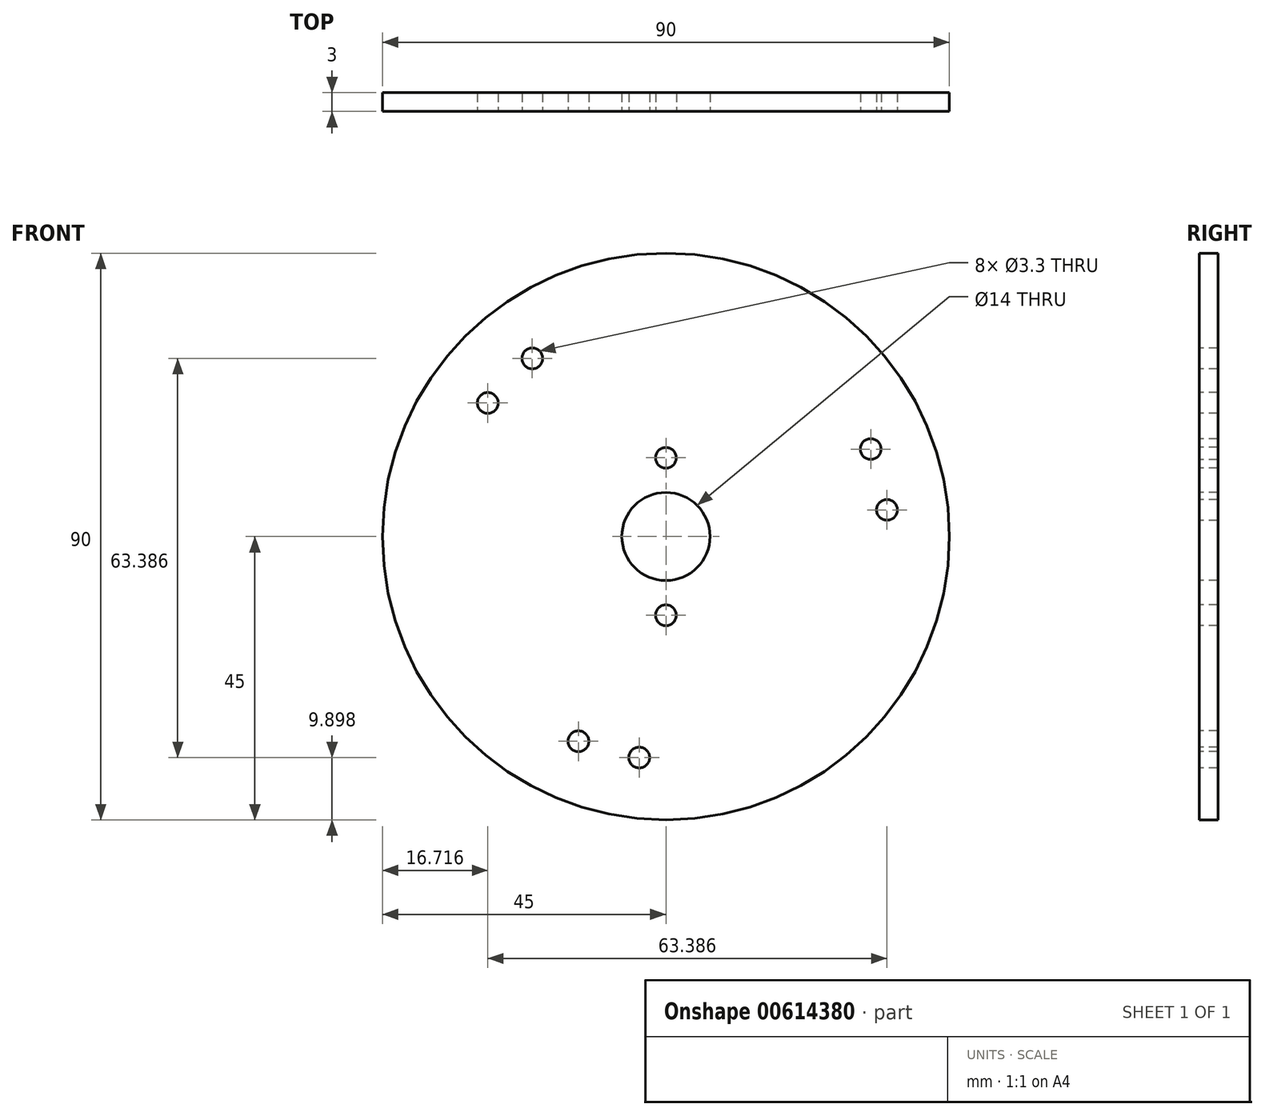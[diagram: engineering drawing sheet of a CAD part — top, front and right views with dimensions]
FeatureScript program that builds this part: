
annotation { "Feature Type Name" : "Feature", "Feature Type Description" : "" }
export const myFeature = defineFeature(function(context is Context, id is Id, definition is map)
    precondition{}
    {
        {
            var Q0;
            Q0=qCreatedBy(makeId("Front.planeOp"),FACE);
            var sketch = newSketch(context, id + "F0", { "sketchPlane" : qUnion([Q0])});
            skCircle(sketch, "E0", {"center": v(0, 0) * mm, "radius": 7 * mm});
            skCircle(sketch, "E1", {"center": v(0, 0) * mm, "radius": 45 * mm});
            skCircle(sketch, "E2", {"center": v(0, 0) * mm, "radius": 23 * mm, "construction": true});
            skLineSegment(sketch, "E3", {"start": v(0, 23) * mm, "end": v(0, 7) * mm, "construction": true});
            skPoint(sketch, "E4", {"position": v(0, 12.5) * mm});
            skPoint(sketch, "E5.1.0", {"position": v(0, -12.5) * mm});
            skLineSegment(sketch, "E6", {"start": v(0, 0) * mm, "end": v(-31.82, 31.82) * mm, "construction": true});
            skCircle(sketch, "E7", {"center": v(0, 0) * mm, "radius": 25 * mm, "construction": true});
            skCircle(sketch, "E8", {"center": v(0, 0) * mm, "radius": 18.5 * mm, "construction": true});
            skPoint(sketch, "E9", {"position": v(-21.21, 28.28) * mm});
            skPoint(sketch, "E10.MirrorP", {"position": v(-28.28, 21.21) * mm});
            skLineSegment(sketch, "E11", {"start": v(-28.28, 21.21) * mm, "end": v(-21.21, 28.28) * mm});
            skPoint(sketch, "E12", {"position": v(-24.75, 24.75) * mm});
            skPoint(sketch, "E13.1.0", {"position": v(-9.06, -33.8) * mm});
            skPoint(sketch, "E13.1.1", {"position": v(-13.89, -32.51) * mm});
            skPoint(sketch, "E13.1.2", {"position": v(-4.23, -35.1) * mm});
            skPoint(sketch, "E13.2.0", {"position": v(33.8, 9.06) * mm});
            skPoint(sketch, "E13.2.1", {"position": v(35.1, 4.23) * mm});
            skPoint(sketch, "E13.2.2", {"position": v(32.51, 13.89) * mm});
            skSolve(sketch);
        }
        {
            var Q0;
            Q0=makeQuery(id+"F0.imprint","IMPRINT",FACE,{"disambiguationData":[TD([[makeQuery(id+"F0.imprint","IMPRINT",EDGE,{"derivedFrom":sQuery(id+"F0.wireOp",EDGE,"E0")}),-1.0]])]});
            extrude(context, id + "F1", {"entities" : qUnion([Q0]), "oppositeDirection" : true, "depth" : 3 * mm, "offsetDistance" : 25 * mm});
        }
        {
            var Q0;
            Q0=sQuery(id+"F0.wireOp",VERTEX,"E9");
            var Q1;
            Q1=sQuery(id+"F0.wireOp",VERTEX,"E10.MirrorP");
            var Q2;
            Q2=sQuery(id+"F0.wireOp",VERTEX,"E13.1.1");
            var Q3;
            Q3=sQuery(id+"F0.wireOp",VERTEX,"E13.1.2");
            var Q4;
            Q4=sQuery(id+"F0.wireOp",VERTEX,"E13.2.1");
            var Q5;
            Q5=sQuery(id+"F0.wireOp",VERTEX,"E13.2.2");
            var Q6;
            Q6=makeQuery(id+"F1.opExtrude","SWEPT_BODY",BODY,{"disambiguationData":[OSD([sQuery(id+"F0.wireOp",EDGE,"E0"),sQuery(id+"F0.wireOp",EDGE,"E1")])]});
            hole(context, id + "F2", {"style" : HoleStyle.SIMPLE, "endStyle" : HoleEndStyle.THROUGH, "standardTappedOrClearance" : lookupTablePath({ "standard" : "ISO", "fit" : "Normal", "size" : "M3", "type" : "Clearance" }), "standardBlindInLast" : lookupTablePath({ "fit" : "Standard", "standard" : "ISO", "size" : "M3", "type" : "Clearance" }), "holeDiameter" : 3.3 * mm, "majorDiameter" : 5 * mm, "isTappedThrough" : true, "tappedDepth" : 12 * mm, "tapClearance" : 3, "locations" : qUnion([Q0, Q1, Q2, Q3, Q4, Q5]), "scope" : qUnion([Q6])});
        }
        {
            var Q0;
            Q0=sQuery(id+"F0.wireOp",VERTEX,"E4");
            var Q1;
            Q1=sQuery(id+"F0.wireOp",VERTEX,"E5.1.0");
            var Q2;
            Q2=makeQuery(id+"F1.opExtrude","SWEPT_BODY",BODY,{"disambiguationData":[OSD([sQuery(id+"F0.wireOp",EDGE,"E0"),sQuery(id+"F0.wireOp",EDGE,"E1")])]});
            hole(context, id + "F3", {"style" : HoleStyle.SIMPLE, "endStyle" : HoleEndStyle.THROUGH, "standardTappedOrClearance" : lookupTablePath({ "standard" : "ISO", "fit" : "Normal", "size" : "M3", "type" : "Clearance" }), "standardBlindInLast" : lookupTablePath({ "fit" : "Standard", "standard" : "ISO", "size" : "M3", "type" : "Clearance" }), "holeDiameter" : 3.3 * mm, "majorDiameter" : 5 * mm, "isTappedThrough" : true, "tappedDepth" : 12 * mm, "tapClearance" : 3, "locations" : qUnion([Q0, Q1]), "scope" : qUnion([Q2])});
        }
    });
